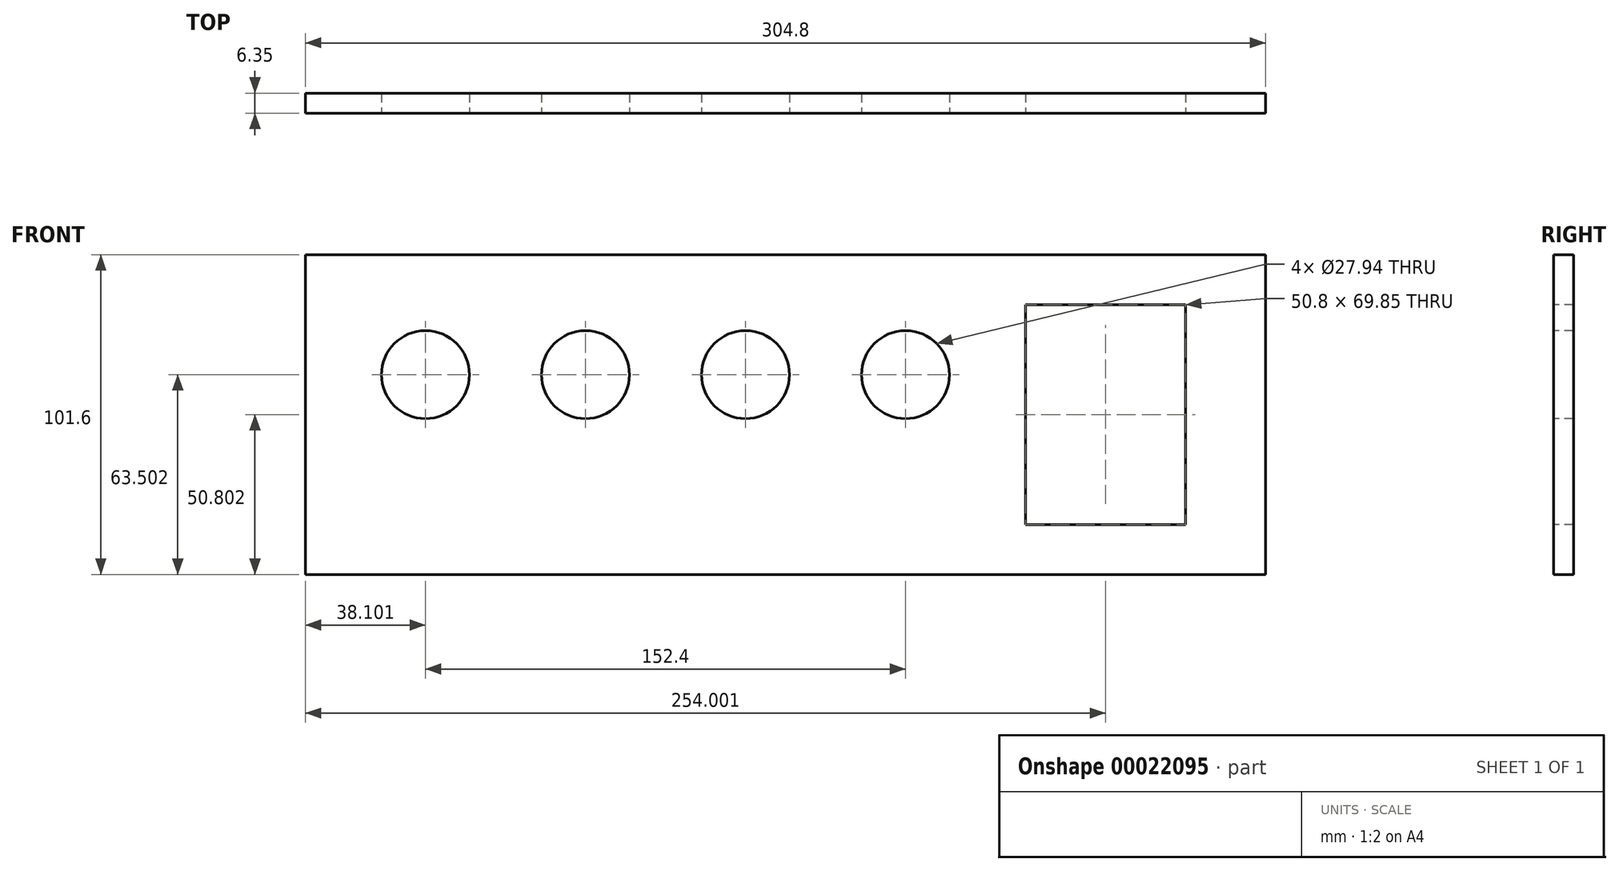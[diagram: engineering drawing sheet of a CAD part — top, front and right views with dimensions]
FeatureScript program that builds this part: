
annotation { "Feature Type Name" : "Feature", "Feature Type Description" : "" }
export const myFeature = defineFeature(function(context is Context, id is Id, definition is map)
    precondition{}
    {
        {
            var Q0;
            Q0=qCreatedBy(makeId("Front.planeOp"),FACE);
            var sketch = newSketch(context, id + "F0", { "sketchPlane" : qUnion([Q0])});
            skLineSegment(sketch, "E0.bottom", {"start": v(-148, 22.04) * mm, "end": v(156.8, 22.04) * mm});
            skLineSegment(sketch, "E0.top", {"start": v(-148, -79.56) * mm, "end": v(156.8, -79.56) * mm});
            skLineSegment(sketch, "E0.left", {"start": v(-148, 22.04) * mm, "end": v(-148, -79.56) * mm});
            skLineSegment(sketch, "E0.right", {"start": v(156.8, 22.04) * mm, "end": v(156.8, -79.56) * mm});
            skSolve(sketch);
        }
        {
            var Q0;
            Q0 = qSketchRegion(id + "F0", true);
            extrude(context, id + "F1", {"entities" : qUnion([Q0]), "depth" : 6.35 * mm});
        }
        {
            var Q0;
            Q0=makeQuery(id+"F1.opExtrude","CAP_FACE",FACE,{"disambiguationData":[OSD([sQuery(id+"F0.wireOp",EDGE,"E0.bottom"),sQuery(id+"F0.wireOp",EDGE,"E0.top"),sQuery(id+"F0.wireOp",EDGE,"E0.left"),sQuery(id+"F0.wireOp",EDGE,"E0.right")])],"isStart":false});
            var sketch = newSketch(context, id + "F2", { "sketchPlane" : qUnion([Q0])});
            skCircle(sketch, "E1", {"center": v(-109.9, -16.06) * mm, "radius": 13.97 * mm});
            skCircle(sketch, "E2.1.0.0", {"center": v(-59.1, -16.06) * mm, "radius": 13.97 * mm});
            skCircle(sketch, "E2.2.0.0", {"center": v(-8.3, -16.06) * mm, "radius": 13.97 * mm});
            skLineSegment(sketch, "E2.direction1", {"start": v(-109.9, -16.06) * mm, "end": v(-59.1, -16.06) * mm, "construction": true});
            skCircle(sketch, "E3.0.3.0", {"center": v(42.5, -16.06) * mm, "radius": 13.97 * mm});
            skSolve(sketch);
        }
        {
            var Q0;
            Q0 = qSketchRegion(id + "F2", true);
            extrude(context, id + "F3", {"entities" : qUnion([Q0]), "operationType" : NewBodyOperationType.REMOVE, "oppositeDirection" : true, "depth" : 25.4 * mm});
        }
        {
            var Q0;
            Q0=makeQuery(id+"F1.opExtrude","CAP_FACE",FACE,{"disambiguationData":[OSD([sQuery(id+"F0.wireOp",EDGE,"E0.bottom"),sQuery(id+"F0.wireOp",EDGE,"E0.top"),sQuery(id+"F0.wireOp",EDGE,"E0.left"),sQuery(id+"F0.wireOp",EDGE,"E0.right")])],"isStart":false});
            var sketch = newSketch(context, id + "F4", { "sketchPlane" : qUnion([Q0])});
            skLineSegment(sketch, "E4.bottom", {"start": v(80.6, 6.17) * mm, "end": v(131.4, 6.17) * mm});
            skLineSegment(sketch, "E4.top", {"start": v(80.6, -63.68) * mm, "end": v(131.4, -63.68) * mm});
            skLineSegment(sketch, "E4.left", {"start": v(80.6, 6.17) * mm, "end": v(80.6, -63.68) * mm});
            skLineSegment(sketch, "E4.right", {"start": v(131.4, 6.17) * mm, "end": v(131.4, -63.68) * mm});
            skSolve(sketch);
        }
        {
            var Q0;
            Q0=makeQuery(id+"F4.imprint","IMPRINT",FACE,{"disambiguationData":[TD([[makeQuery(id+"F4.imprint","IMPRINT",EDGE,{"derivedFrom":sQuery(id+"F4.wireOp",EDGE,"E4.bottom")}),-1.0]])]});
            extrude(context, id + "F5", {"entities" : qUnion([Q0]), "operationType" : NewBodyOperationType.REMOVE, "oppositeDirection" : true, "depth" : 25.4 * mm});
        }
    });
